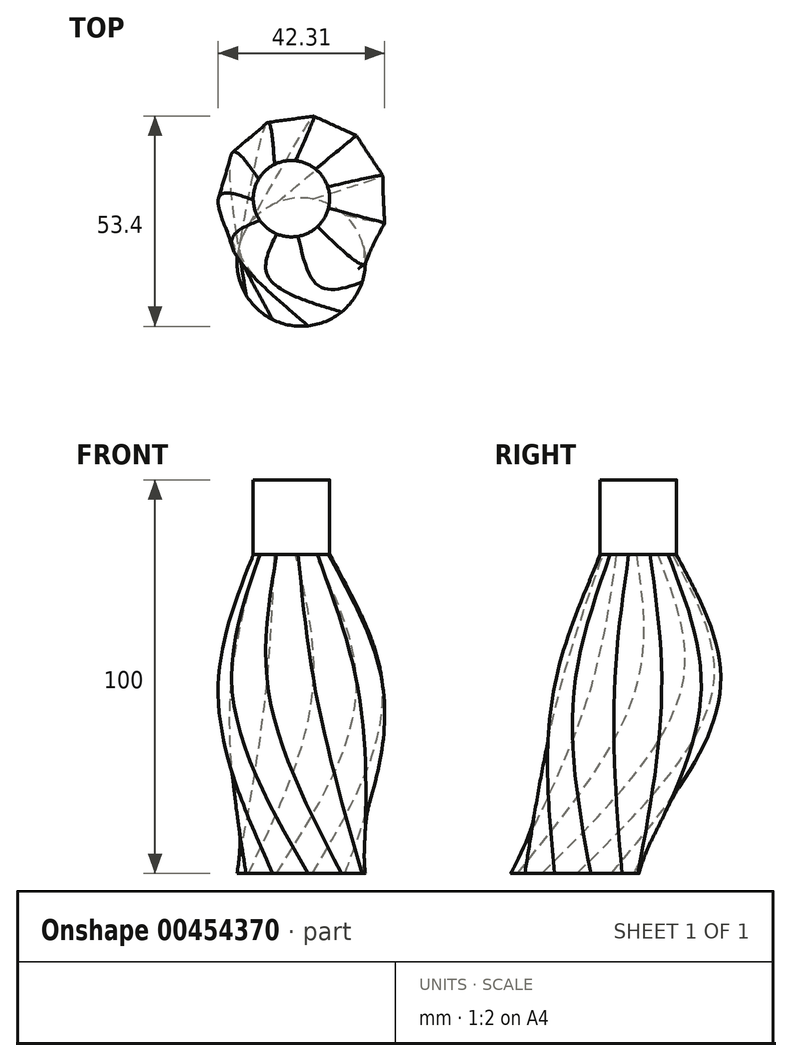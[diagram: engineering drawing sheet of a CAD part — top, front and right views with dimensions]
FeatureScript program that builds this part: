
annotation { "Feature Type Name" : "Feature", "Feature Type Description" : "" }
export const myFeature = defineFeature(function(context is Context, id is Id, definition is map)
    precondition{}
    {
        {
            var Q0;
            Q0=qCreatedBy(makeId("Top.planeOp"),FACE);
            var sketch = newSketch(context, id + "F0", { "sketchPlane" : qUnion([Q0])});
            skCircle(sketch, "E0", {"center": v(2.48, -16.11) * mm, "radius": 16.3 * mm});
            skPoint(sketch, "E0.first.point", {"position": v(0, 0) * mm});
            skPoint(sketch, "E0.second.point", {"position": v(17.06, -23.4) * mm});
            skPoint(sketch, "E0.third.point", {"position": v(-10.52, -25.95) * mm});
            skSolve(sketch);
        }
        {
            var Q0;
            Q0=qCreatedBy(makeId("Top.planeOp"),FACE);
            cPlane(context, id + "F1", {"entities" : qUnion([Q0]), "cplaneType" : CPlaneType.OFFSET, "offset" : 49 * mm, "width" : 150 * mm, "height" : 150 * mm});
        }
        {
            var Q0;
            Q0=qCreatedBy(id+"F1.planeOp",FACE);
            var sketch = newSketch(context, id + "F2", { "sketchPlane" : qUnion([Q0])});
            skCircle(sketch, "E1.cCircle", {"center": v(2.64, 0) * mm, "radius": 20.33 * mm, "construction": true});
            skLineSegment(sketch, "E1.0", {"start": v(22.97, 5.97) * mm, "end": v(22.97, -5.97) * mm});
            skLineSegment(sketch, "E1.1", {"start": v(22.97, -5.97) * mm, "end": v(16.51, -16.02) * mm});
            skLineSegment(sketch, "E1.2", {"start": v(16.51, -16.02) * mm, "end": v(5.65, -20.98) * mm});
            skLineSegment(sketch, "E1.3", {"start": v(5.65, -20.98) * mm, "end": v(-6.17, -19.28) * mm});
            skLineSegment(sketch, "E1.4", {"start": v(-6.17, -19.28) * mm, "end": v(-15.2, -11.46) * mm});
            skLineSegment(sketch, "E1.5", {"start": v(-15.2, -11.46) * mm, "end": v(-18.56, 0) * mm});
            skLineSegment(sketch, "E1.6", {"start": v(-18.56, 0) * mm, "end": v(-15.2, 11.46) * mm});
            skLineSegment(sketch, "E1.7", {"start": v(-15.2, 11.46) * mm, "end": v(-6.17, 19.28) * mm});
            skLineSegment(sketch, "E1.8", {"start": v(-6.17, 19.28) * mm, "end": v(5.65, 20.98) * mm});
            skLineSegment(sketch, "E1.9", {"start": v(5.65, 20.98) * mm, "end": v(16.51, 16.02) * mm});
            skLineSegment(sketch, "E1.10", {"start": v(16.51, 16.02) * mm, "end": v(22.97, 5.97) * mm});
            skPoint(sketch, "E1.0.midPoint", {"position": v(22.97, 0) * mm});
            skSolve(sketch);
        }
        {
            var Q0;
            Q0=qCreatedBy(id+"F1.planeOp",FACE);
            cPlane(context, id + "F3", {"entities" : qUnion([Q0]), "cplaneType" : CPlaneType.OFFSET, "offset" : 32 * mm, "width" : 150 * mm, "height" : 150 * mm});
        }
        {
            var Q0;
            Q0=qCreatedBy(id+"F3.planeOp",FACE);
            var sketch = newSketch(context, id + "F4", { "sketchPlane" : qUnion([Q0])});
            skCircle(sketch, "E2", {"center": v(0, 0) * mm, "radius": 9.7 * mm});
            skSolve(sketch);
        }
        {
            var Q0;
            Q0=makeQuery(id+"F0.imprint","IMPRINT",FACE,{"disambiguationData":[TD([[makeQuery(id+"F0.imprint","IMPRINT",EDGE,{"derivedFrom":sQuery(id+"F0.wireOp",EDGE,"E0")}),1.0]])]});
            var Q1;
            Q1=makeQuery(id+"F2.imprint","IMPRINT",FACE,{"disambiguationData":[TD([[makeQuery(id+"F2.imprint","IMPRINT",EDGE,{"derivedFrom":sQuery(id+"F2.wireOp",EDGE,"E1.0")}),-1.0]])]});
            var Q2;
            Q2=makeQuery(id+"F4.imprint","IMPRINT",FACE,{"disambiguationData":[TD([[makeQuery(id+"F4.imprint","IMPRINT",EDGE,{"derivedFrom":sQuery(id+"F4.wireOp",EDGE,"E2")}),1.0]])]});
            loft(context, id + "F5", {"sheetProfilesArray" : [{ "sheetProfileEntities" : qUnion([Q0]) }, { "sheetProfileEntities" : qUnion([Q1]) }, { "sheetProfileEntities" : qUnion([Q2]) }]});
        }
        {
            var Q0;
            Q0=makeQuery(id+"F5.opLoft","CAP_FACE",FACE,{"disambiguationData":[OSD([makeQuery(id+"F4.imprint","IMPRINT",FACE,{"disambiguationData":[TD([[makeQuery(id+"F4.imprint","IMPRINT",EDGE,{"derivedFrom":sQuery(id+"F4.wireOp",EDGE,"E2")}),1.0]])]})])],"isStart":true});
            extrude(context, id + "F6", {"entities" : qUnion([Q0]), "operationType" : NewBodyOperationType.ADD, "depth" : 19 * mm});
        }
    });
